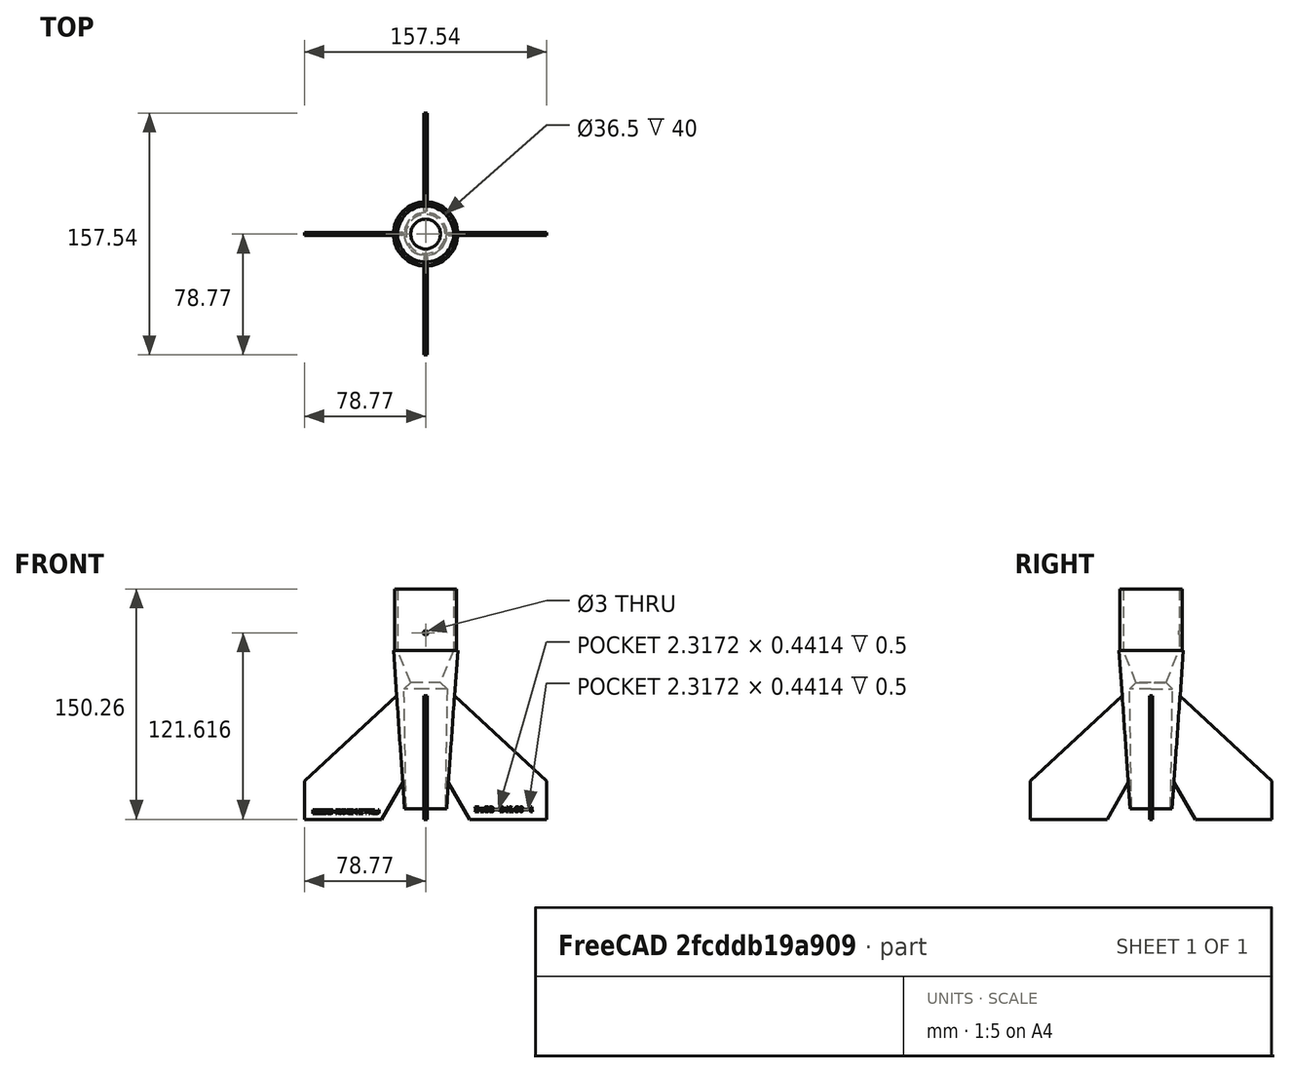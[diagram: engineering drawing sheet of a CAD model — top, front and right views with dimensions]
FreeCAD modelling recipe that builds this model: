
FCSTD DOCUMENT  (FreeCAD 0.20R29603 (Git))
Label: Ez3D-24L60-4v3
License: All rights reserved
LicenseURL: http://en.wikipedia.org/wiki/All_rights_reserved
objects: Sketcher::SketchObject×3, Part::Part2DObjectPython×2, PartDesign::Pocket×2, PartDesign::Revolution×1, PartDesign::Pad×1, PartDesign::PolarPattern×1, PartDesign::Hole×1, PartDesign::Body×1, Mesh::Feature×1
note: 17 computed .brp shape members not serialized (recipe doc carries the construction recipe); baked Part::Feature solids carry a one-line shape summary decoded from their .brp

FEATURE [Sketcher::SketchObject] Sketch  label="Motor Mount"
  FullyConstrained = false
  MapMode = 5
  Placement = pos=(0,0,0) rot=(1,0,0;1.5708rad)
  Support = -> [XZ_Plane]
  sketch-geometry (9):
    g0: LineSegment StartX=12.7 StartY=7 StartZ=0 EndX=13.7 EndY=7 EndZ=0
    g1: LineSegment StartX=13.7 StartY=7 StartZ=0 EndX=20.95 EndY=110.264 EndZ=0
    g2: LineSegment StartX=9.7 StartY=89.3 StartZ=0 EndX=14 EndY=85 EndZ=0
    g3: LineSegment StartX=14 StartY=85 StartZ=0 EndX=12.7 EndY=7 EndZ=0
    g4: LineSegment StartX=18.25 StartY=150.264 StartZ=0 EndX=18.25 EndY=110.264 EndZ=0
    g5: LineSegment StartX=18.25 StartY=110.264 StartZ=0 EndX=9.7 EndY=89.3 EndZ=0
    g6: LineSegment StartX=20.95 StartY=110.264 StartZ=0 EndX=20.25 EndY=110.264 EndZ=0
    g7: LineSegment StartX=20.25 StartY=110.264 StartZ=0 EndX=20.25 EndY=150.264 EndZ=0
    g8: LineSegment StartX=20.25 StartY=150.264 StartZ=0 EndX=18.25 EndY=150.264 EndZ=0
  constraints (26):
    c: Coincident(g0,g1)
    c: Coincident(g2,g3)
    c: Coincident(g3,g0)
    c: DistanceX(g0,g0) = 1
    c: DistanceX(g-1,g0) = 12.7
    c: Angle(g2) = -0.785398
    c: Vertical(g4)
    c: Coincident(g4,g5)
    c: Coincident(g6,g7)
    c: Vertical(g7)
    c: Coincident(g7,g8)
    c: Coincident(g8,g4)
    c: Horizontal(g8)
    c: Horizontal(g6)
    c: DistanceX(g-1,g7) = 20.25
    c: DistanceX(g8,g8) = 2
    c: Horizontal(g4,g6)
    c: DistanceY(g4,g4) = 40
    c: DistanceX(g6,g6) = 0.7
    c: Coincident(g5,g2)
    c: Coincident(g1,g6)
    c: DistanceY(g-1,g0) = 7
    c: Horizontal(g0)
    c: DistanceX(g-1,g2) = 14
    c: DistanceX(g-1,g2) = 9.7
    c: DistanceY(g3,g3) = 78
FEATURE [PartDesign::Revolution] Revolution  label="Motor Mount001"
  Angle = 360
  Axis = (0,-2e-16,1)
  Base = (0,0,0)
  Placement = pos=(0,0,0) rot=(1,0,0;1.5708rad)
  Profile = -> Sketch
  ReferenceAxis = -> Sketch [V_Axis]
  Reversed = true
FEATURE [Sketcher::SketchObject] Sketch001  label="Fin"
  FullyConstrained = false
  MapMode = 5
  Placement = pos=(0,0,0) rot=(1,0,0;1.5708rad)
  Support = -> [XZ_Plane]
  sketch-geometry (5):
    g0: LineSegment StartX=28.7659 StartY=0 StartZ=0 EndX=78.7659 EndY=0 EndZ=0
    g1: LineSegment StartX=78.7659 StartY=0 StartZ=0 EndX=78.7659 EndY=25 EndZ=0
    g2: LineSegment StartX=78.7659 StartY=25 StartZ=0 EndX=14 EndY=85 EndZ=0
    g3: LineSegment StartX=14 StartY=85 StartZ=0 EndX=14 EndY=25.5753 EndZ=0
    g4: LineSegment StartX=14 StartY=25.5753 StartZ=0 EndX=28.7659 EndY=0 EndZ=0
  constraints (13):
    c: Coincident(g0,g1)
    c: Coincident(g1,g2)
    c: Vertical(g1)
    c: Coincident(g2,g3)
    c: Vertical(g3)
    c: Coincident(g3,g4)
    c: Coincident(g0,g4)
    c: DistanceX(g-1,g2) = 14
    c: Angle(g4) = -1.0472
    c: DistanceX(g0,g0) = 50
    c: DistanceY(g1,g1) = 25
    c: DistanceY(g1,g2) = 60
    c: Tangent(g0,g-1)
FEATURE [PartDesign::Pad] Pad  label="Fin001"
  BaseFeature = -> Revolution
  Direction = (0,-1,-2e-16)
  Length = 2
  Length2 = 100
  Midplane = true
  Placement = pos=(0,0,0) rot=(1,0,0;1.5708rad)
  Profile = -> Sketch001
  Type = 0
FEATURE [PartDesign::PolarPattern] PolarPattern  label="Fins"
  Angle = 360
  Axis = -> Z_Axis
  BaseFeature = -> Pad
  Occurrences = 4
  Originals = -> [Pad]
  Placement = pos=(0,0,0) rot=(1,0,0;1.5708rad)
FEATURE [Sketcher::SketchObject] Sketch002
  FullyConstrained = false
  MapMode = 5
  Placement = pos=(0,0,0) rot=(1,0,0;1.5708rad)
  Support = -> [XZ_Plane]
  sketch-geometry (1):
    g0: Circle CenterX=0 CenterY=121.616 CenterZ=0 NormalX=0 NormalY=0 NormalZ=1 AngleXU=0 Radius=3.43919
  constraints (1):
    c: PointOnObject(g0,g-2)
FEATURE [PartDesign::Hole] Hole
  BaseFeature = -> PolarPattern
  CustomThreadClearance = 0
  Depth = 25
  DepthType = 0
  Diameter = 3
  DrillForDepth = false
  DrillPoint = 1
  DrillPointAngle = 118
  HoleCutCountersinkAngle = 90
  HoleCutCustomValues = false
  HoleCutDepth = 0
  HoleCutDiameter = 6.1
  HoleCutType = 0
  ModelThread = false
  Placement = pos=(0,0,0) rot=(1,0,0;1.5708rad)
  Profile = -> Sketch002
  Tapered = false
  TaperedAngle = 90
  ThreadClass = 0
  ThreadDepth = 25
  ThreadDepthType = 0
  ThreadDirection = 0
  ThreadFit = 0
  ThreadSize = 0
  ThreadType = 0
  Threaded = false
  UseCustomThreadClearance = false
FEATURE [Part::Part2DObjectPython] ShapeString  label="Logo"  # Draft 2D object (typed FeaturePython)
  FontFile = <path>
  MakeFace = true
  Placement = pos=(-73.619,-1,3.905) rot=(1,0,0;1.5708rad)
  Size = 1.4
  String = Ez3D Rocketry
  Tracking = 0
FEATURE [Part::Part2DObjectPython] ShapeString001  label="PN"  # Draft 2D object (typed FeaturePython)
  FontFile = <path>
  MakeFace = true
  Placement = pos=(31.958,-1,4.973) rot=(1,0,0;1.5708rad)
  Size = 4
  String = Ez3D-24L60-4
  Tracking = 0
FEATURE [PartDesign::Pocket] Pocket
  BaseFeature = -> Hole
  Direction = (2e-16,1,-7e-16)
  Length = 0.5
  Length2 = 5
  Placement = pos=(0,0,0) rot=(1,0,0;1.5708rad)
  Profile = -> ShapeString
  ReferenceAxis = -> ShapeString [N_Axis]
  Type = 0
FEATURE [PartDesign::Pocket] Pocket001
  BaseFeature = -> Pocket
  Direction = (2e-16,1,-7e-16)
  Length = 0.5
  Length2 = 5
  Placement = pos=(0,0,0) rot=(1,0,0;1.5708rad)
  Profile = -> ShapeString001
  ReferenceAxis = -> ShapeString001 [N_Axis]
  Type = 0
FEATURE [PartDesign::Body] Body
  Group = -> [Sketch,Revolution,Sketch001,Pad,PolarPattern,Sketch002,Hole,ShapeString,ShapeString001,Pocket,Pocket001]
  Origin = -> Origin
  Tip = -> Pocket001
FEATURE [Mesh::Feature] For24mm_M30x2__10mm_high___12_25_radius  label="For24mm M30x2 -10mm high - 12.25 radius"
note: 2 file-system paths scrubbed to <path> (originals preserved in the JSON sidecar)
